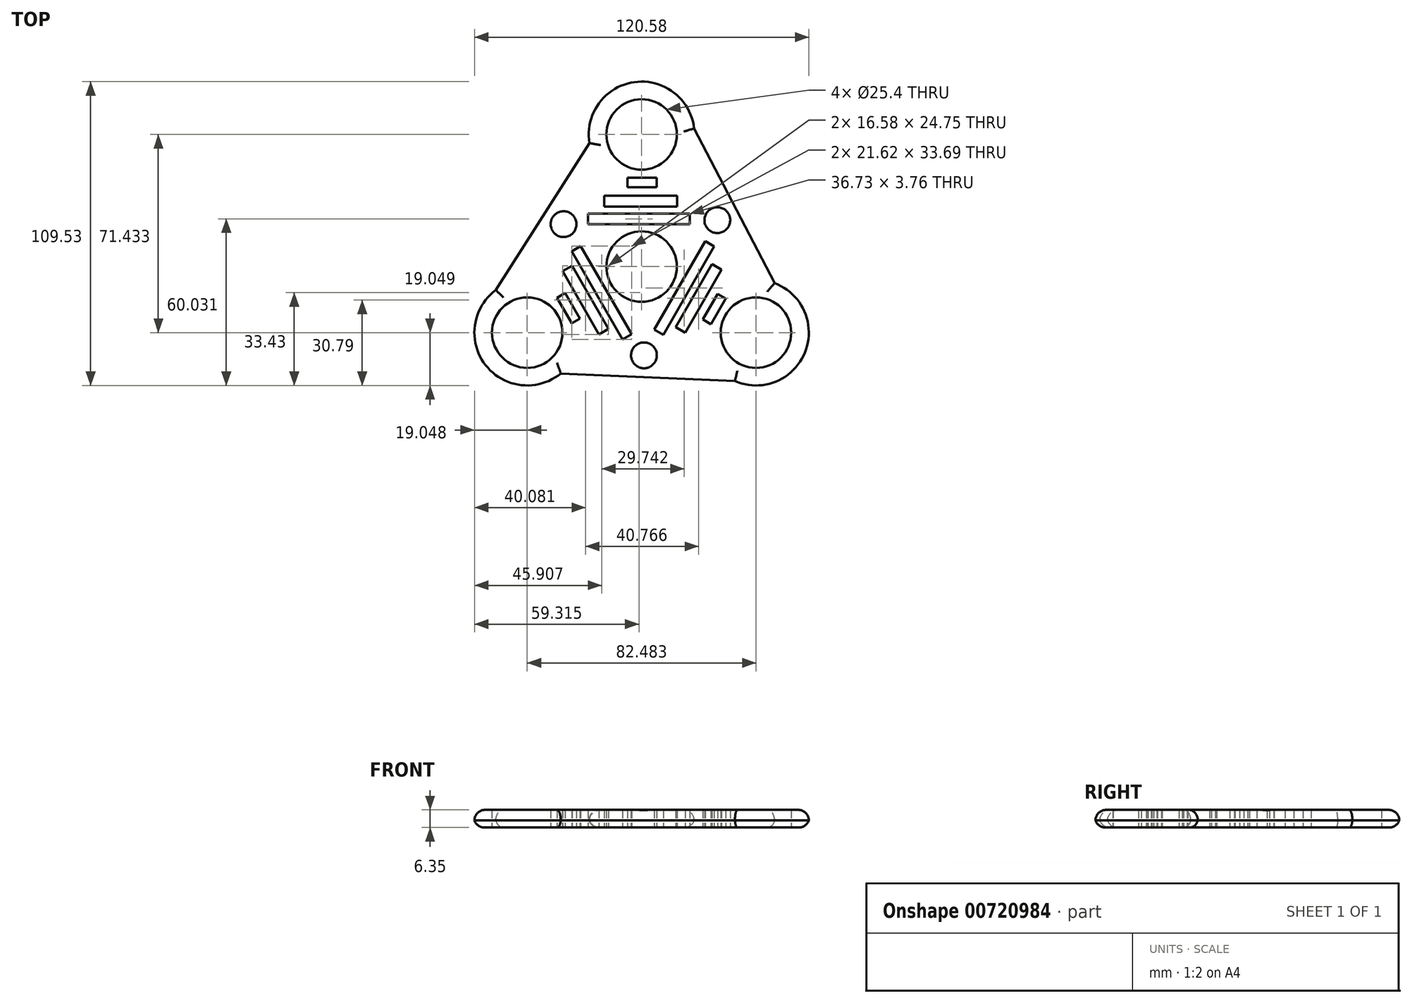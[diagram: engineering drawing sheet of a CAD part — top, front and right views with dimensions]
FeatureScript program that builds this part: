
annotation { "Feature Type Name" : "Feature", "Feature Type Description" : "" }
export const myFeature = defineFeature(function(context is Context, id is Id, definition is map)
    precondition{}
    {
        {
            var Q0;
            Q0=qCreatedBy(makeId("Top.planeOp"),FACE);
            var sketch = newSketch(context, id + "F0", { "sketchPlane" : qUnion([Q0])});
            skCircle(sketch, "E0", {"center": v(0, 0) * mm, "radius": 12.7 * mm});
            skCircle(sketch, "E1", {"center": v(0, 47.62) * mm, "radius": 12.7 * mm});
            skCircle(sketch, "E2.1.1", {"center": v(-41.24, -23.81) * mm, "radius": 12.7 * mm});
            skCircle(sketch, "E2.2.1", {"center": v(41.24, -23.81) * mm, "radius": 12.7 * mm});
            skArc(sketch, "E3", {"start": v(-52.57, -8.5) * mm, "mid": v(-56.26, -35.53) * mm, "end": v(-29.15, -38.53) * mm});
            skArc(sketch, "E4.1.0", {"start": v(33.65, -41.28) * mm, "mid": v(58.9, -30.96) * mm, "end": v(47.94, -5.98) * mm});
            skArc(sketch, "E4.2.0", {"start": v(18.93, 49.78) * mm, "mid": v(-2.63, 66.49) * mm, "end": v(-18.8, 44.51) * mm});
            skLineSegment(sketch, "E5", {"start": v(-52.57, -8.5) * mm, "end": v(-18.8, 44.51) * mm});
            skLineSegment(sketch, "E6", {"start": v(18.93, 49.78) * mm, "end": v(47.94, -5.98) * mm});
            skLineSegment(sketch, "E7", {"start": v(33.65, -41.28) * mm, "end": v(-29.15, -38.53) * mm});
            skLineSegment(sketch, "E8.bottom", {"start": v(-5.15, 31.99) * mm, "end": v(5.5, 31.99) * mm});
            skLineSegment(sketch, "E8.top", {"start": v(-5.15, 28.65) * mm, "end": v(5.5, 28.65) * mm});
            skLineSegment(sketch, "E8.left", {"start": v(-5.15, 31.99) * mm, "end": v(-5.15, 28.65) * mm});
            skLineSegment(sketch, "E8.right", {"start": v(5.5, 31.99) * mm, "end": v(5.5, 28.65) * mm});
            skLineSegment(sketch, "E9.bottom", {"start": v(-13.5, 21.55) * mm, "end": v(12.8, 21.55) * mm});
            skLineSegment(sketch, "E9.top", {"start": v(-13.5, 25.52) * mm, "end": v(12.8, 25.52) * mm});
            skLineSegment(sketch, "E9.left", {"start": v(-13.5, 21.55) * mm, "end": v(-13.5, 25.52) * mm});
            skLineSegment(sketch, "E9.right", {"start": v(12.8, 21.55) * mm, "end": v(12.8, 25.52) * mm});
            skLineSegment(sketch, "E10.bottom", {"start": v(-19.34, 15.3) * mm, "end": v(17.4, 15.3) * mm});
            skLineSegment(sketch, "E10.top", {"start": v(-19.34, 19.05) * mm, "end": v(17.4, 19.05) * mm});
            skLineSegment(sketch, "E10.left", {"start": v(-19.34, 15.3) * mm, "end": v(-19.34, 19.05) * mm});
            skLineSegment(sketch, "E10.right", {"start": v(17.4, 15.3) * mm, "end": v(17.4, 19.05) * mm});
            skLineSegment(sketch, "E11.1.0", {"start": v(-3.57, -24.4) * mm, "end": v(-21.94, 7.41) * mm});
            skLineSegment(sketch, "E11.1.1", {"start": v(-3.57, -24.4) * mm, "end": v(-6.83, -26.27) * mm});
            skLineSegment(sketch, "E11.1.2", {"start": v(-6.83, -26.27) * mm, "end": v(-25.2, 5.54) * mm});
            skLineSegment(sketch, "E11.1.3", {"start": v(-21.94, 7.41) * mm, "end": v(-25.2, 5.54) * mm});
            skLineSegment(sketch, "E11.1.4", {"start": v(-11.92, -22.47) * mm, "end": v(-25.07, 0.3) * mm});
            skLineSegment(sketch, "E11.1.5", {"start": v(-11.92, -22.47) * mm, "end": v(-15.35, -24.45) * mm});
            skLineSegment(sketch, "E11.1.6", {"start": v(-15.35, -24.45) * mm, "end": v(-28.5, -1.68) * mm});
            skLineSegment(sketch, "E11.1.7", {"start": v(-25.07, 0.3) * mm, "end": v(-28.5, -1.68) * mm});
            skLineSegment(sketch, "E11.1.8", {"start": v(-22.24, -18.78) * mm, "end": v(-27.56, -9.57) * mm});
            skLineSegment(sketch, "E11.1.9", {"start": v(-25.13, -20.45) * mm, "end": v(-22.24, -18.78) * mm});
            skLineSegment(sketch, "E11.1.10", {"start": v(-25.13, -20.45) * mm, "end": v(-30.45, -11.24) * mm});
            skLineSegment(sketch, "E11.1.11", {"start": v(-30.45, -11.24) * mm, "end": v(-27.56, -9.57) * mm});
            skLineSegment(sketch, "E11.2.0", {"start": v(22.91, 9.1) * mm, "end": v(4.55, -22.7) * mm});
            skLineSegment(sketch, "E11.2.1", {"start": v(22.91, 9.1) * mm, "end": v(26.17, 7.22) * mm});
            skLineSegment(sketch, "E11.2.2", {"start": v(26.17, 7.22) * mm, "end": v(7.8, -24.59) * mm});
            skLineSegment(sketch, "E11.2.3", {"start": v(4.55, -22.7) * mm, "end": v(7.8, -24.59) * mm});
            skLineSegment(sketch, "E11.2.4", {"start": v(25.41, 0.91) * mm, "end": v(12.27, -21.86) * mm});
            skLineSegment(sketch, "E11.2.5", {"start": v(25.41, 0.91) * mm, "end": v(28.85, -1.07) * mm});
            skLineSegment(sketch, "E11.2.6", {"start": v(28.85, -1.07) * mm, "end": v(15.7, -23.84) * mm});
            skLineSegment(sketch, "E11.2.7", {"start": v(12.27, -21.86) * mm, "end": v(15.7, -23.84) * mm});
            skLineSegment(sketch, "E11.2.8", {"start": v(27.39, -9.87) * mm, "end": v(22.06, -19.08) * mm});
            skLineSegment(sketch, "E11.2.9", {"start": v(30.28, -11.54) * mm, "end": v(27.39, -9.87) * mm});
            skLineSegment(sketch, "E11.2.10", {"start": v(30.28, -11.54) * mm, "end": v(24.96, -20.75) * mm});
            skLineSegment(sketch, "E11.2.11", {"start": v(24.96, -20.75) * mm, "end": v(22.06, -19.08) * mm});
            skCircle(sketch, "E12", {"center": v(27.3, 16.73) * mm, "radius": 4.65 * mm});
            skCircle(sketch, "E13.1.0", {"center": v(-28.14, 15.27) * mm, "radius": 4.65 * mm});
            skCircle(sketch, "E13.2.0", {"center": v(0.84, -32) * mm, "radius": 4.65 * mm});
            skSolve(sketch);
        }
        {
            var Q0;
            Q0 = qSketchRegion(id + "F0", true);
            extrude(context, id + "F1", {"entities" : qUnion([Q0]), "depth" : 6.35 * mm, "offsetDistance" : 25.4 * mm});
        }
        {
            var Q0;
            Q0=makeQuery(id+"F1.opExtrude","CAP_EDGE",EDGE,{"disambiguationData":[OSD([sQuery(id+"F0.wireOp",EDGE,"E5")])],"isStart":false});
            var Q1;
            Q1=makeQuery(id+"F1.opExtrude","CAP_EDGE",EDGE,{"disambiguationData":[OSD([sQuery(id+"F0.wireOp",EDGE,"E4.2.0")])],"isStart":false});
            var Q2;
            Q2=makeQuery(id+"F1.opExtrude","CAP_EDGE",EDGE,{"disambiguationData":[OSD([sQuery(id+"F0.wireOp",EDGE,"E6")])],"isStart":false});
            var Q3;
            Q3=makeQuery(id+"F1.opExtrude","CAP_EDGE",EDGE,{"disambiguationData":[OSD([sQuery(id+"F0.wireOp",EDGE,"E4.1.0")])],"isStart":false});
            var Q4;
            Q4=makeQuery(id+"F1.opExtrude","CAP_EDGE",EDGE,{"disambiguationData":[OSD([sQuery(id+"F0.wireOp",EDGE,"E7")])],"isStart":false});
            var Q5;
            Q5=makeQuery(id+"F1.opExtrude","CAP_EDGE",EDGE,{"disambiguationData":[OSD([sQuery(id+"F0.wireOp",EDGE,"E3")])],"isStart":false});
            fillet(context, id + "F2", {"entities" : qUnion([Q0, Q1, Q2, Q3, Q4, Q5]), "radius" : 3.8 * mm, "tangentPropagation" : true, "allowEdgeOverflow" : false});
        }
        {
            var Q0;
            Q0=makeQuery(id+"F1.opExtrude","CAP_EDGE",EDGE,{"disambiguationData":[OSD([sQuery(id+"F0.wireOp",EDGE,"E4.2.0")])],"isStart":true});
            var Q1;
            Q1=makeQuery(id+"F1.opExtrude","CAP_EDGE",EDGE,{"disambiguationData":[OSD([sQuery(id+"F0.wireOp",EDGE,"E5")])],"isStart":true});
            var Q2;
            Q2=makeQuery(id+"F1.opExtrude","CAP_EDGE",EDGE,{"disambiguationData":[OSD([sQuery(id+"F0.wireOp",EDGE,"E3")])],"isStart":true});
            var Q3;
            Q3=makeQuery(id+"F1.opExtrude","CAP_EDGE",EDGE,{"disambiguationData":[OSD([sQuery(id+"F0.wireOp",EDGE,"E7")])],"isStart":true});
            var Q4;
            Q4=makeQuery(id+"F1.opExtrude","CAP_EDGE",EDGE,{"disambiguationData":[OSD([sQuery(id+"F0.wireOp",EDGE,"E4.1.0")])],"isStart":true});
            var Q5;
            Q5=makeQuery(id+"F1.opExtrude","CAP_EDGE",EDGE,{"disambiguationData":[OSD([sQuery(id+"F0.wireOp",EDGE,"E6")])],"isStart":true});
            fillet(context, id + "F3", {"entities" : qUnion([Q0, Q1, Q2, Q3, Q4, Q5]), "radius" : 3.8 * mm, "tangentPropagation" : true, "allowEdgeOverflow" : false});
        }
    });
